# Revit family: Doors_Fire-Doors-Shutters_Overhead-Door-Corporation_Fire-Rated-Counter-Doors-641_
name_source: partatom
category: Specialty Equipment
units: mm (PartAtom-declared; Revit-internal decimal feet)

## family parameters
Always vertical = Yes
Cut with Voids When Loaded = Yes
Host = Wall
OmniClass Number = 23.30.10.21.34
OmniClass Title = Industrial Doors
Part Type = Normal
Room Calculation Point = No
Round Connector Dimension = Use Diameter
Shared = No

## types (9) — shared parameters
Description = Model 641 Fire Rated Rolling Counter Door
Finish Material = Finish - Overhead Door - Black
Manufacturer = Overhead Door Corporation
Model = 641
Powder Coat (Note) = PowderGuard® Premium powder coat finish options are available in approximately 200 colors as well as custom matching to specification.
Power Factor = 1
Product Guid = 1411a188-1ec4-42e9-a969-e61c85bce94a
Product Page URL = https://www.overheaddoor.com
Product data url = https://www.bimobject.com
URL = https://www.overheaddoor.com
Wall Closure = By host

## per-type parameters (varying)
| type | Apparent Load Phase 1 | Apparent Load Phase 2 | Apparent Load Phase 3 | CDX | Crank | Current | Frequency | Manual | Number of Poles | Voltage |
| 115 volts, one phase, 60 Hz (110-120V range) | 2300 VA | 0 VA | 0 VA | Yes | No | 20 A | 60 Hz | No | 1 | 115 V |
| 208 volts, one phase, 60 Hz (190-207V range) | 4160 VA | 0 VA | 0 VA | Yes | No | 20 A | 60 Hz | No | 1 | 208 V |
| 208 volts, three phase, 60 Hz (190-207 V range) | 2402 VA | 2402 VA | 2402 VA | Yes | No | 20 A | 60 Hz | No | 3 | 208 V |
| 230 volts, one phase, 60 Hz (208-245V range) | 4600 VA | 0 VA | 0 VA | Yes | No | 20 A | 60 Hz | No | 1 | 230 V |
| 230 volts, three phase, 60 Hz (208-245 V range) | 2656 VA | 2656 VA | 2656 VA | Yes | No | 20 A | 60 Hz | No | 3 | 230 V |
| 460 volts, three phase, 60 Hz (456-495 V range) | 5312 VA | 5312 VA | 5312 VA | Yes | No | 20 A | 60 Hz | No | 3 | 460 V |
| 575 volts, three phase, 60 Hz | 6640 VA | 6640 VA | 6640 VA | Yes | No | 20 A | 60 Hz | No | 3 | 575 V |
| Manual push-up | 0 VA | 0 VA | 0 VA | No | No | 0 A | 0 Hz | Yes | 1 | 0 V |
| Manual crank | 0 VA | 0 VA | 0 VA | No | Yes | 0 A | 0 Hz | No | 1 | 0 V |

## geometry (parser evidence)
native form markers: Sweep x9
no freeform markers — native parametric forms only
